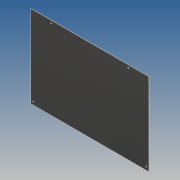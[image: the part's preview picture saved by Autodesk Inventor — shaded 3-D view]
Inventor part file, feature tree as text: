
AUTODESK INVENTOR PART (.ipt)
format: ipt  version: 2019 (Build 230136000, 136)  size: 99,840 bytes
history: native  units: mm
features: sketch x2, extrude x1, hole x1, projected_geometry x1
ambient origin geometry x8: Origin, YZ Plane, XZ Plane, XY Plane, X Axis, Y Axis, Z Axis, Center Point
bodies: Solid1 (feature_tree)
feature tree (5):
  extrude  "Extrusion1"  Depth=575.0mm
  hole  "Hole1"  [1 undecoded]
  sketch  "Sketch1"  dims[d0=400.0mm d1=575.0mm]
  sketch  "Sketch2"  dims[d2=2.0mm d3=0.0mm d4=12.5mm d5=12.5mm d6=12.5mm d7=100.0mm d8=100.0mm d9=15.0mm d11=6.0mm d12=6.0mm d13=4.0mm d14=2.0mm d15=90.0deg d16=10.0mm d17=20.594885mm d18=12.5mm d19=15.0mm]
  projected_geometry  "Projected Loop1"
note: 1 required parameter value undecoded (feature->parameter linkage not recoverable at this tier; creation-order binding heuristic only, values carry confidence <= 0.55)
